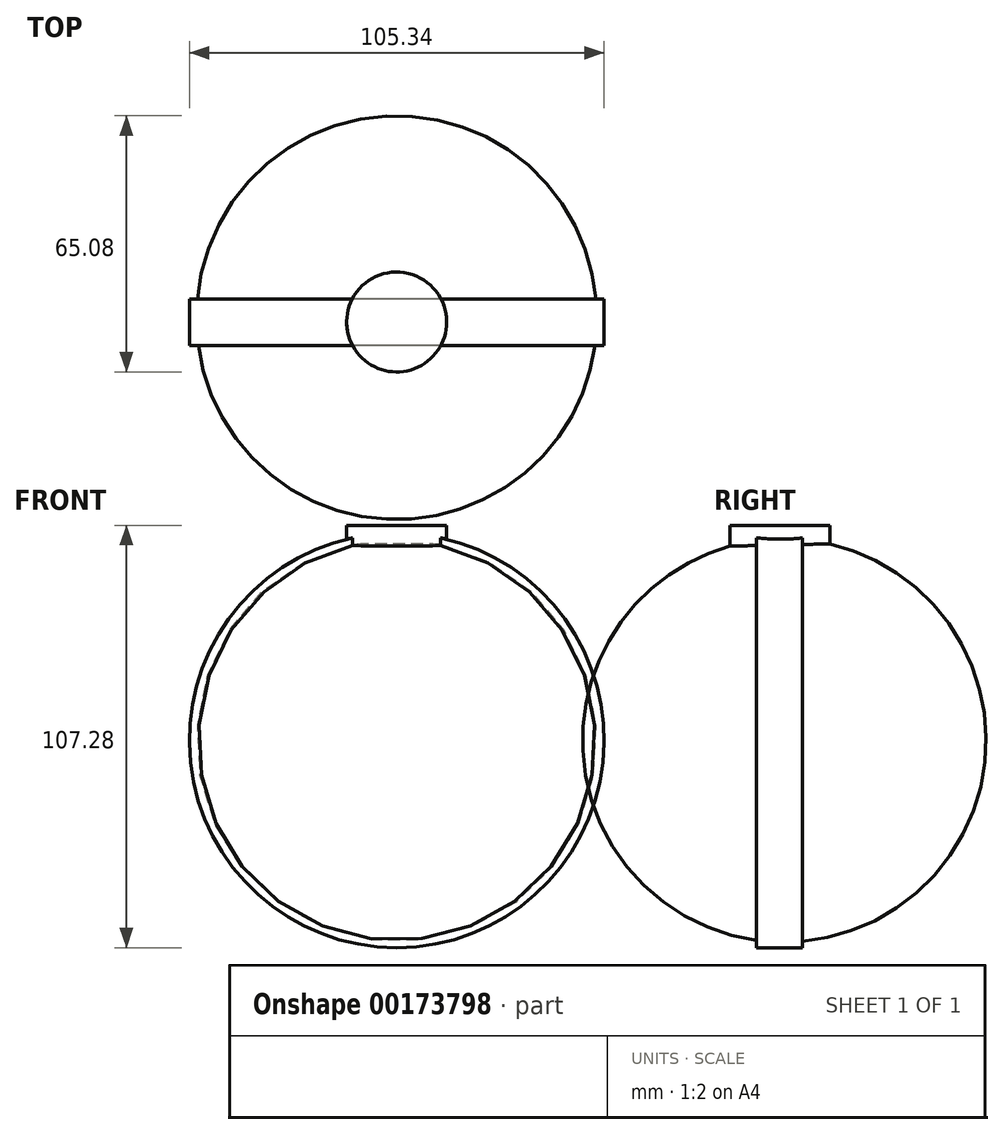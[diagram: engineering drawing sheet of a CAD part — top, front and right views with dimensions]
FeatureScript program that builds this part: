
annotation { "Feature Type Name" : "Feature", "Feature Type Description" : "" }
export const myFeature = defineFeature(function(context is Context, id is Id, definition is map)
    precondition{}
    {
        {
            var Q0;
            Q0=qCreatedBy(makeId("Top.planeOp"),FACE);
            var sketch = newSketch(context, id + "F0", { "sketchPlane" : qUnion([Q0])});
            skArc(sketch, "E0", {"start": v(50.8, 0.96) * mm, "mid": v(0.15, 52.38) * mm, "end": v(-50.8, 1.26) * mm});
            skLineSegment(sketch, "E1", {"start": v(-50.8, 1.26) * mm, "end": v(50.8, 0.96) * mm});
            skSolve(sketch);
        }
        {
            var Q0;
            Q0=makeQuery(id+"F0.imprint","IMPRINT",FACE,{"disambiguationData":[TD([[makeQuery(id+"F0.imprint","IMPRINT",EDGE,{"derivedFrom":sQuery(id+"F0.wireOp",EDGE,"E0")}),1.0]])]});
            var Q1;
            Q1=sQuery(id+"F0.wireOp",EDGE,"E1");
            revolve(context, id + "F1", {"entities" : qUnion([Q0]), "axis" : qUnion([Q1]), "revolveType" : RevolveType.FULL});
        }
        {
            var Q0;
            Q0=qCreatedBy(makeId("Top.planeOp"),FACE);
            var sketch = newSketch(context, id + "F2", { "sketchPlane" : qUnion([Q0])});
            skCircle(sketch, "E2", {"center": v(0, 0) * mm, "radius": 12.7 * mm});
            skSolve(sketch);
        }
        {
            var Q0;
            Q0 = qSketchRegion(id + "F2", true);
            extrude(context, id + "F3", {"entities" : qUnion([Q0]), "operationType" : NewBodyOperationType.ADD, "depth" : 54.6 * mm});
        }
        {
            var Q0;
            Q0=qCreatedBy(makeId("Top.planeOp"),FACE);
            var sketch = newSketch(context, id + "F4", { "sketchPlane" : qUnion([Q0])});
            skLineSegment(sketch, "E3", {"start": v(-10.88, 5.78) * mm, "end": v(-52.67, 5.78) * mm});
            skLineSegment(sketch, "E4", {"start": v(-52.67, 5.78) * mm, "end": v(-52.67, -6.01) * mm});
            skLineSegment(sketch, "E5", {"start": v(-52.67, -6.01) * mm, "end": v(-52.67, -6.01) * mm});
            skLineSegment(sketch, "E6", {"start": v(-52.67, -6.01) * mm, "end": v(-52.67, 5.78) * mm});
            skLineSegment(sketch, "E7", {"start": v(-10.88, 5.78) * mm, "end": v(-10.88, -6.01) * mm});
            skLineSegment(sketch, "E8", {"start": v(-10.88, -6.01) * mm, "end": v(-52.67, -6.01) * mm});
            skLineSegment(sketch, "E9", {"start": v(0, 5.78) * mm, "end": v(0, -5.47) * mm});
            skSolve(sketch);
        }
        {
            var Q0;
            Q0 = qSketchRegion(id + "F4", true);
            var Q1;
            Q1=sQuery(id+"F4.wireOp",EDGE,"E9");
            revolve(context, id + "F5", {"operationType" : NewBodyOperationType.ADD, "entities" : qUnion([Q0]), "axis" : qUnion([Q1]), "revolveType" : RevolveType.FULL});
        }
    });
